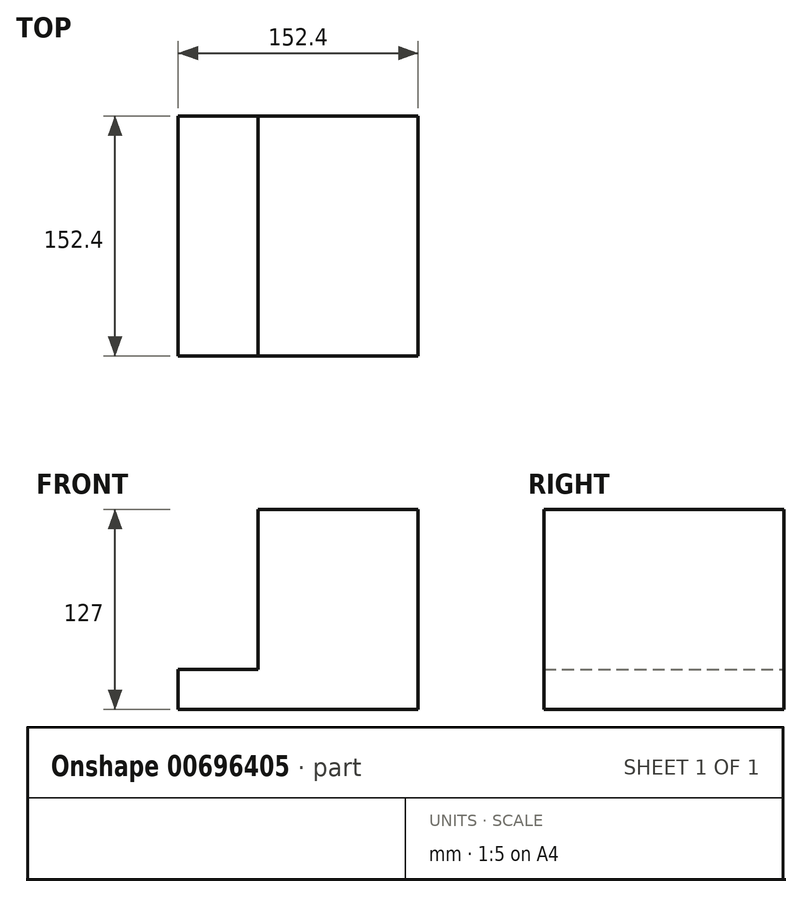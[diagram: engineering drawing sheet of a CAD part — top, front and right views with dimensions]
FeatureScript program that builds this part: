
annotation { "Feature Type Name" : "Feature", "Feature Type Description" : "" }
export const myFeature = defineFeature(function(context is Context, id is Id, definition is map)
    precondition{}
    {
        {
            var Q0;
            Q0=qCreatedBy(makeId("Front.planeOp"),FACE);
            var sketch = newSketch(context, id + "F0", { "sketchPlane" : qUnion([Q0])});
            skLineSegment(sketch, "E0", {"start": v(-75.42, 0) * mm, "end": v(76.98, 0) * mm});
            skLineSegment(sketch, "E1", {"start": v(-75.42, 0) * mm, "end": v(-75.42, 25.4) * mm});
            skLineSegment(sketch, "E2", {"start": v(-75.42, 25.4) * mm, "end": v(-24.62, 25.4) * mm});
            skLineSegment(sketch, "E3", {"start": v(-24.62, 25.4) * mm, "end": v(-24.62, 127) * mm});
            skLineSegment(sketch, "E4", {"start": v(-24.62, 127) * mm, "end": v(76.98, 127) * mm});
            skLineSegment(sketch, "E5", {"start": v(76.98, 127) * mm, "end": v(76.98, 0) * mm});
            skSolve(sketch);
        }
        {
            var Q0;
            Q0=makeQuery(id+"F0.imprint","IMPRINT",FACE,{"disambiguationData":[TD([[makeQuery(id+"F0.imprint","IMPRINT",EDGE,{"derivedFrom":sQuery(id+"F0.wireOp",EDGE,"E0")}),1.0]])]});
            extrude(context, id + "F1", {"entities" : qUnion([Q0]), "depth" : 152.4 * mm, "offsetDistance" : 25.4 * mm});
        }
    });
